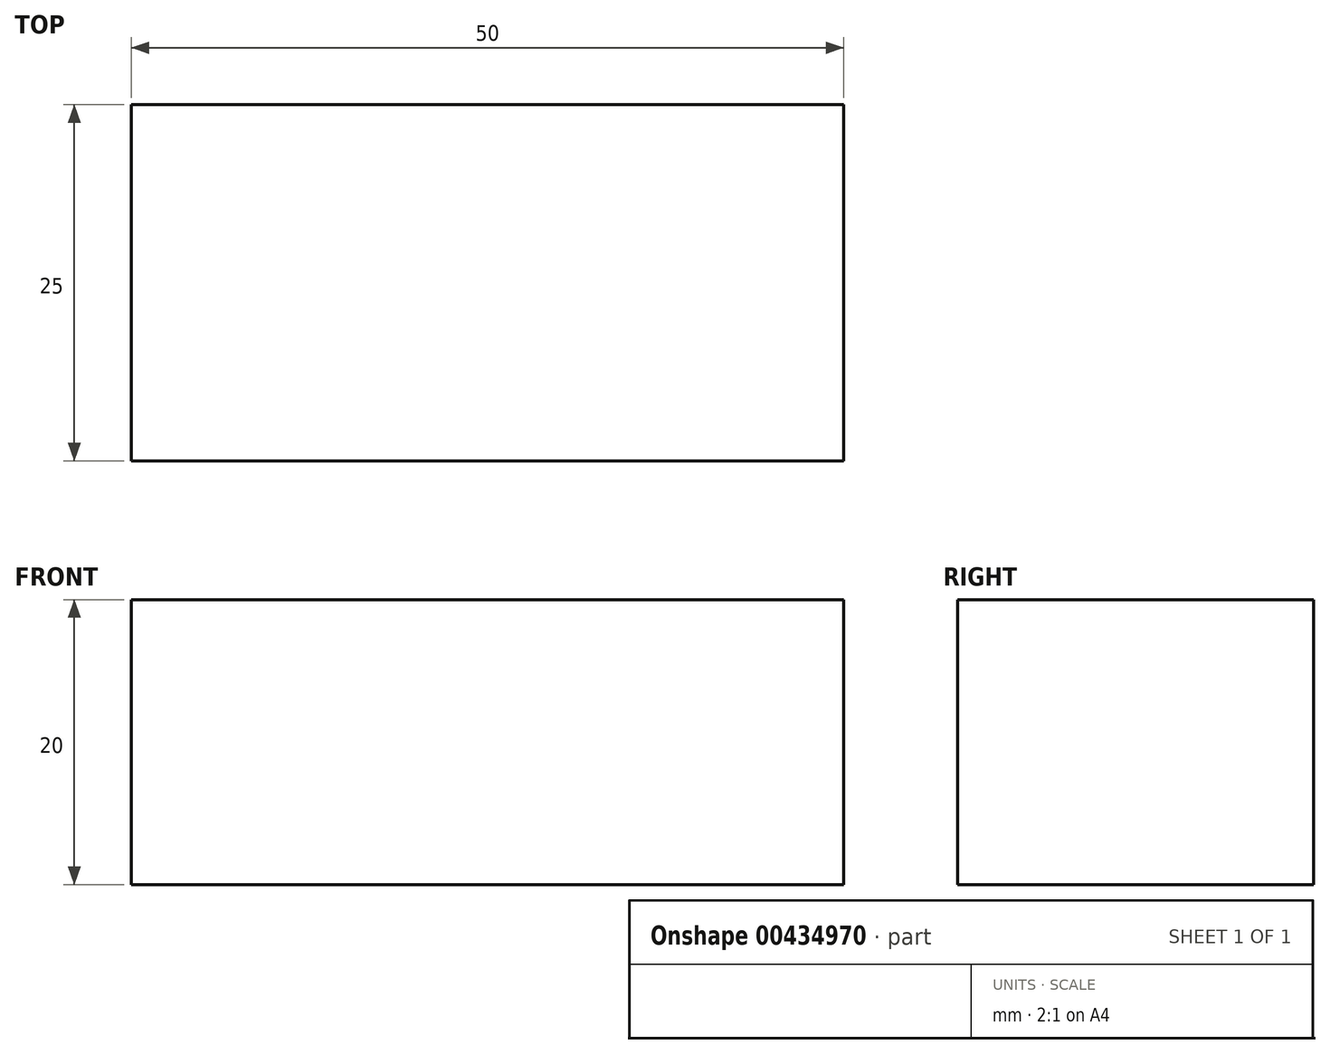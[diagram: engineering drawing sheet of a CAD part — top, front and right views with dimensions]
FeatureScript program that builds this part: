
annotation { "Feature Type Name" : "Feature", "Feature Type Description" : "" }
export const myFeature = defineFeature(function(context is Context, id is Id, definition is map)
    precondition{}
    {
        {
            var Q0;
            Q0=qCreatedBy(makeId("Front.planeOp"),FACE);
            var sketch = newSketch(context, id + "F0", { "sketchPlane" : qUnion([Q0])});
            skLineSegment(sketch, "E0.bottom", {"start": v(25, -10) * mm, "end": v(-25, -10) * mm});
            skLineSegment(sketch, "E0.top", {"start": v(25, 10) * mm, "end": v(-25, 10) * mm});
            skLineSegment(sketch, "E0.left", {"start": v(25, -10) * mm, "end": v(25, 10) * mm});
            skLineSegment(sketch, "E0.right", {"start": v(-25, -10) * mm, "end": v(-25, 10) * mm});
            skPoint(sketch, "E0.middle", {"position": v(0, 0) * mm});
            skLineSegment(sketch, "E1.bottom", {"start": v(34.66, 40) * mm, "end": v(53.98, 40) * mm});
            skLineSegment(sketch, "E1.top", {"start": v(34.66, 15) * mm, "end": v(53.98, 15) * mm});
            skLineSegment(sketch, "E1.left", {"start": v(34.66, 40) * mm, "end": v(34.66, 15) * mm});
            skLineSegment(sketch, "E1.right", {"start": v(53.98, 40) * mm, "end": v(53.98, 15) * mm});
            skPoint(sketch, "E1.middle", {"position": v(44.32, 27.5) * mm});
            skLineSegment(sketch, "E2", {"start": v(25, 10) * mm, "end": v(25, 27.5) * mm});
            skPoint(sketch, "E2.endSnap0", {"position": v(34.66, 27.5) * mm});
            skArc(sketch, "E3", {"start": v(25, 27.5) * mm, "mid": v(27.04, 32.41) * mm, "end": v(31.95, 34.45) * mm});
            skLineSegment(sketch, "E4", {"start": v(31.95, 34.45) * mm, "end": v(44.9, 34.45) * mm});
            skLineSegment(sketch, "E5.0", {"start": v(28.95, 38.76) * mm, "end": v(41.9, 38.76) * mm});
            skArc(sketch, "E5.1", {"start": v(17.7, 27.5) * mm, "mid": v(21, 35.46) * mm, "end": v(28.95, 38.76) * mm});
            skLineSegment(sketch, "E5.2", {"start": v(17.7, 10) * mm, "end": v(17.7, 27.5) * mm});
            skSolve(sketch);
        }
        {
            var Q0;
            Q0=makeQuery(id+"F0.imprint","IMPRINT",FACE,{"disambiguationData":[TD([[makeQuery(id+"F0.imprint","IMPRINT",EDGE,{"derivedFrom":sQuery(id+"F0.wireOp",EDGE,"E0.bottom")}),-1.0]])]});
            extrude(context, id + "F1", {"entities" : qUnion([Q0]), "endBound" : BoundingType.SYMMETRIC, "depth" : 25 * mm});
        }
    });
